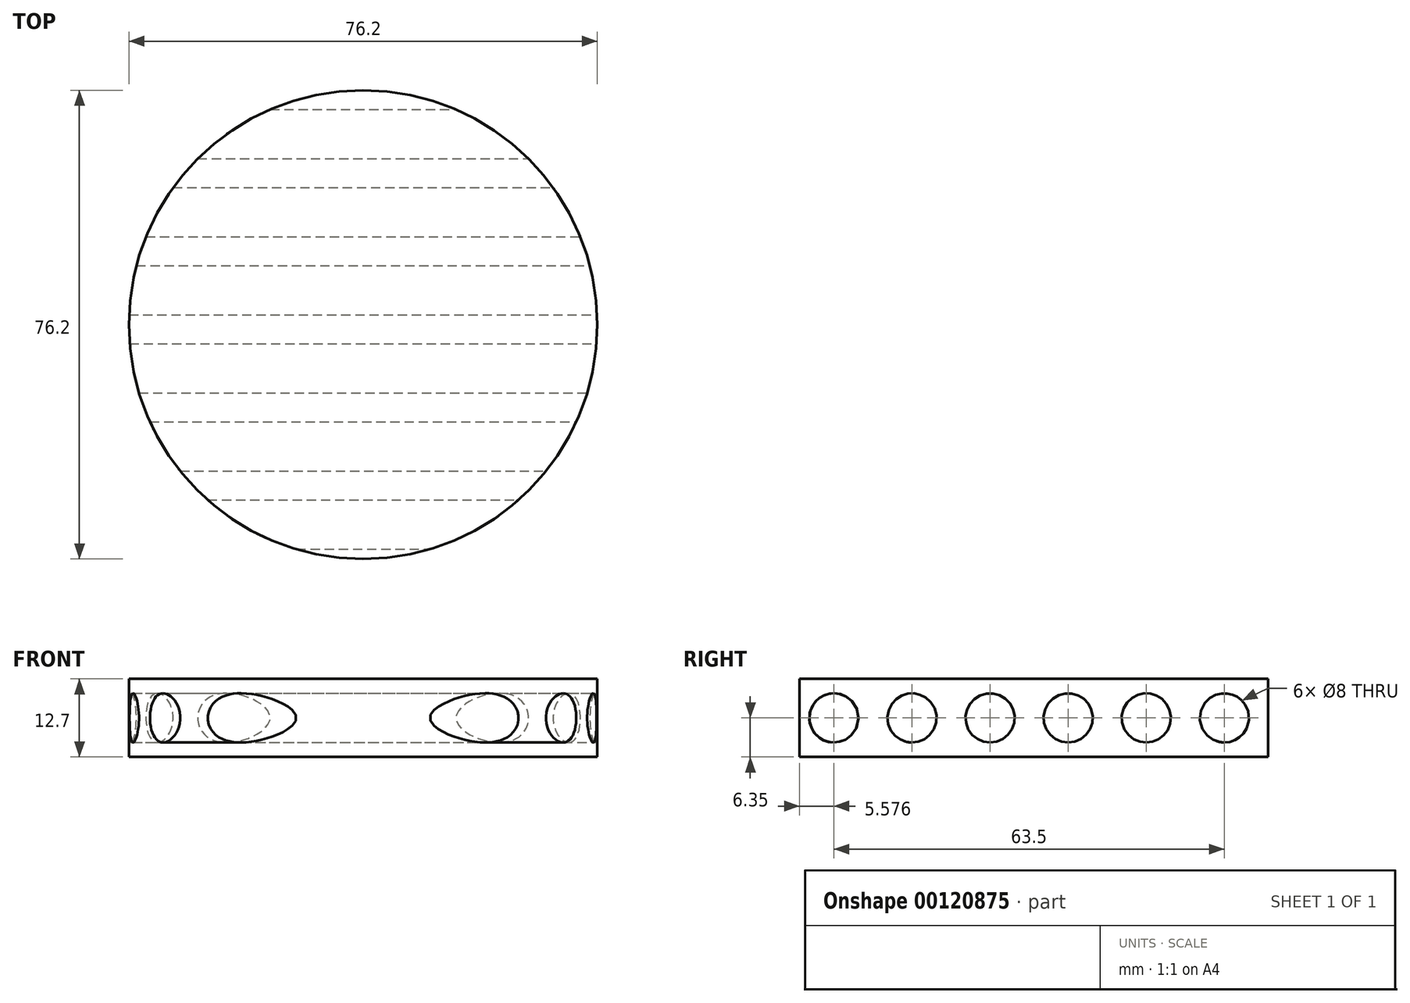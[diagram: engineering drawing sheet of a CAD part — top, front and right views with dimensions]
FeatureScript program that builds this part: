
annotation { "Feature Type Name" : "Feature", "Feature Type Description" : "" }
export const myFeature = defineFeature(function(context is Context, id is Id, definition is map)
    precondition{}
    {
        {
            var Q0;
            Q0=qCreatedBy(makeId("Top.planeOp"),FACE);
            var sketch = newSketch(context, id + "F0", { "sketchPlane" : qUnion([Q0])});
            skCircle(sketch, "E0", {"center": v(0, 0) * mm, "radius": 38.1 * mm});
            skSolve(sketch);
        }
        {
            var Q0;
            Q0 = qSketchRegion(id + "F0", true);
            extrude(context, id + "F1", {"entities" : qUnion([Q0]), "depth" : 12.7 * mm});
        }
        {
            var Q0;
            Q0=qCreatedBy(makeId("Right.planeOp"),FACE);
            var sketch = newSketch(context, id + "F2", { "sketchPlane" : qUnion([Q0])});
            skCircle(sketch, "E1", {"center": v(-32.52, 6.35) * mm, "radius": 4 * mm});
            skCircle(sketch, "E2.1.0.0", {"center": v(-19.82, 6.35) * mm, "radius": 4 * mm});
            skCircle(sketch, "E2.2.0.0", {"center": v(-7.12, 6.35) * mm, "radius": 4 * mm});
            skCircle(sketch, "E2.3.0.0", {"center": v(5.58, 6.35) * mm, "radius": 4 * mm});
            skCircle(sketch, "E2.4.0.0", {"center": v(18.28, 6.35) * mm, "radius": 4 * mm});
            skCircle(sketch, "E2.5.0.0", {"center": v(30.98, 6.35) * mm, "radius": 4 * mm});
            skLineSegment(sketch, "E2.direction1", {"start": v(-32.52, 6.35) * mm, "end": v(-19.82, 6.35) * mm, "construction": true});
            skSolve(sketch);
        }
        {
            var Q0;
            Q0 = qSketchRegion(id + "F2", true);
            extrude(context, id + "F3", {"entities" : qUnion([Q0]), "operationType" : NewBodyOperationType.REMOVE, "endBound" : BoundingType.SYMMETRIC, "oppositeDirection" : true, "depth" : 100 * mm});
        }
    });
